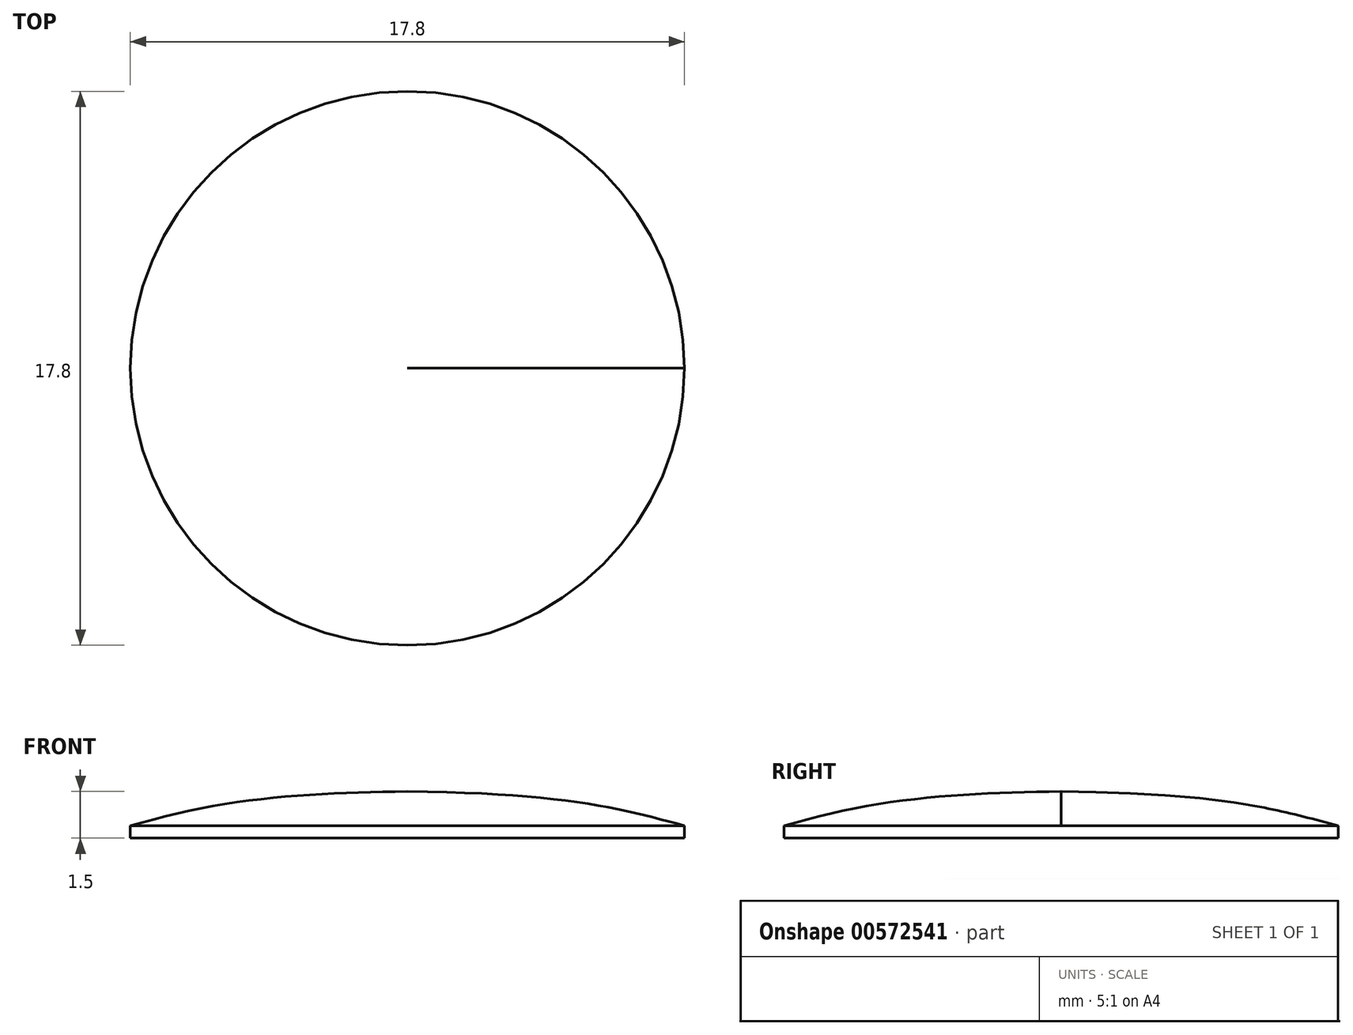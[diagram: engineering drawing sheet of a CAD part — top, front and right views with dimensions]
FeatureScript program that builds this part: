
annotation { "Feature Type Name" : "Feature", "Feature Type Description" : "" }
export const myFeature = defineFeature(function(context is Context, id is Id, definition is map)
    precondition{}
    {
        {
            var Q0;
            Q0=qCreatedBy(makeId("Front.planeOp"),FACE);
            var sketch = newSketch(context, id + "F0", { "sketchPlane" : qUnion([Q0])});
            skLineSegment(sketch, "E0", {"start": v(8.9, 0) * mm, "end": v(0, 0) * mm});
            skLineSegment(sketch, "E1", {"start": v(8.9, 0) * mm, "end": v(8.9, 0.4) * mm});
            skLineSegment(sketch, "E2", {"start": v(0, 0) * mm, "end": v(0, 1.5) * mm});
            skFitSpline(sketch, "E3", {"points": [v(0, 1.5) * mm, v(8.9, 0.4) * mm], "startDerivative": vector(15.34, -0.15) * mm, "endDerivative": vector(5.92, -1.6) * mm});
            skSolve(sketch);
        }
        {
            var Q0;
            Q0=makeQuery(id+"F0.imprint","IMPRINT",FACE,{"disambiguationData":[TD([[makeQuery(id+"F0.imprint","IMPRINT",EDGE,{"derivedFrom":sQuery(id+"F0.wireOp",EDGE,"E0")}),-1.0]])]});
            var Q1;
            Q1=sQuery(id+"F0.wireOp",EDGE,"E2");
            revolve(context, id + "F1", {"entities" : qUnion([Q0]), "axis" : qUnion([Q1]), "revolveType" : RevolveType.FULL});
        }
    });
